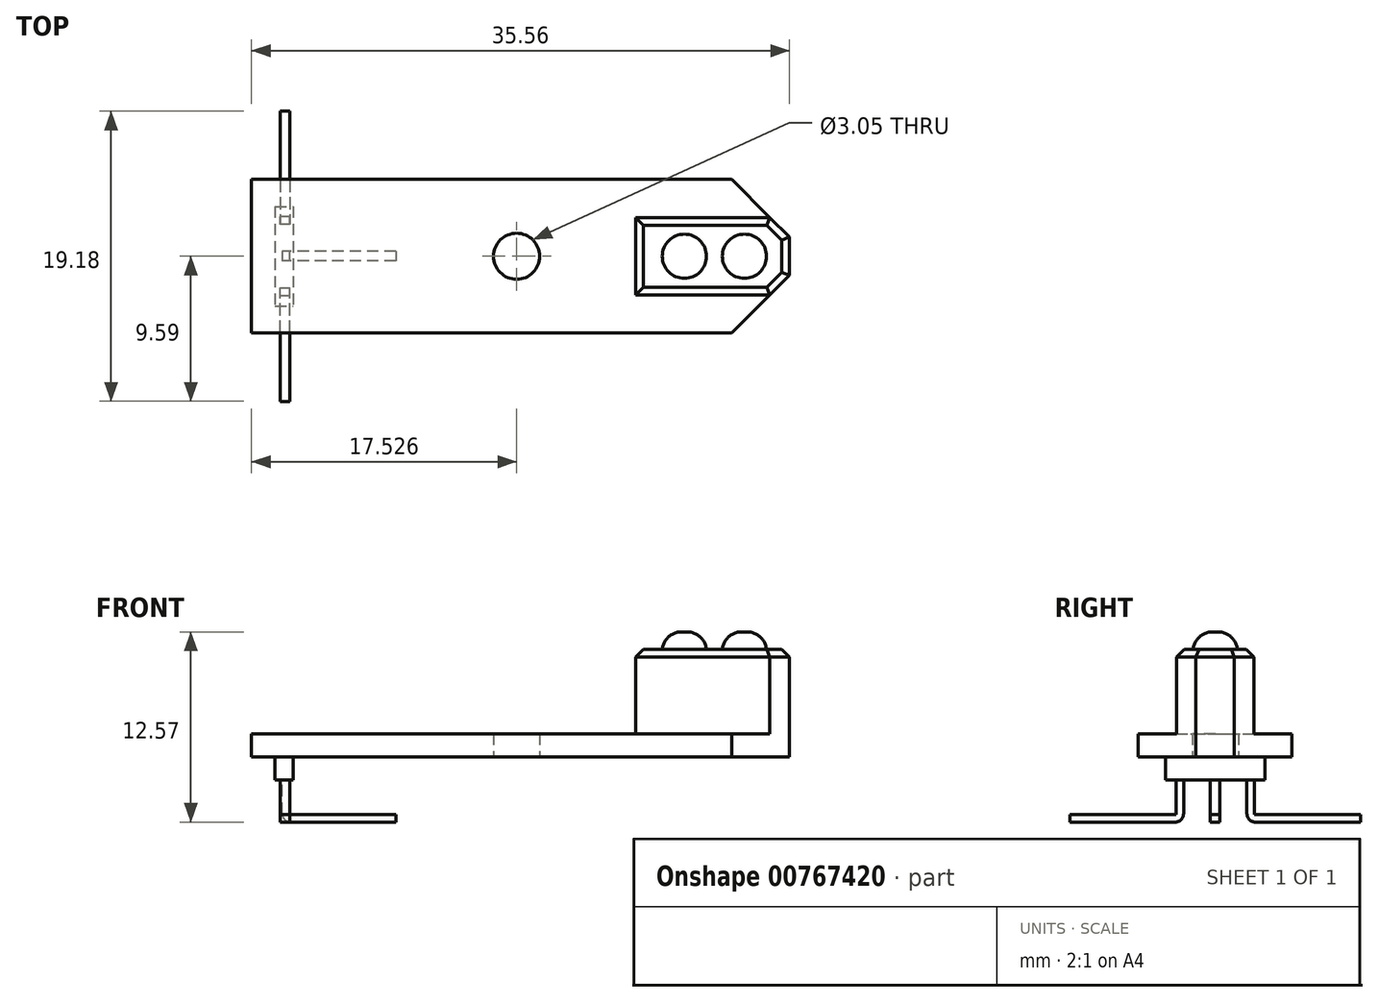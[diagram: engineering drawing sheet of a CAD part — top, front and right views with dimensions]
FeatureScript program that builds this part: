
annotation { "Feature Type Name" : "Feature", "Feature Type Description" : "" }
export const myFeature = defineFeature(function(context is Context, id is Id, definition is map)
    precondition{}
    {
        {
            var Q0;
            Q0=qCreatedBy(makeId("Top.planeOp"),FACE);
            var sketch = newSketch(context, id + "F0", { "sketchPlane" : qUnion([Q0])});
            skLineSegment(sketch, "E0.bottom", {"start": v(13.97, -5.08) * mm, "end": v(-17.78, -5.08) * mm});
            skLineSegment(sketch, "E0.top", {"start": v(13.97, 5.08) * mm, "end": v(-17.78, 5.08) * mm});
            skLineSegment(sketch, "E0.left", {"start": v(17.78, -1.27) * mm, "end": v(17.78, 1.27) * mm});
            skLineSegment(sketch, "E0.right", {"start": v(-17.78, -5.08) * mm, "end": v(-17.78, 5.08) * mm});
            skPoint(sketch, "E0.middle", {"position": v(0, 0) * mm});
            skLineSegment(sketch, "E1", {"start": v(13.97, 5.08) * mm, "end": v(17.78, 1.27) * mm});
            skLineSegment(sketch, "E2", {"start": v(0, 0) * mm, "end": v(10.97, 0) * mm, "construction": true});
            skLineSegment(sketch, "E3.MirrorCS", {"start": v(13.97, -5.08) * mm, "end": v(17.78, -1.27) * mm});
            skPoint(sketch, "E4.orphan", {"position": v(17.78, 5.08) * mm});
            skPoint(sketch, "E5.orphan", {"position": v(17.78, -5.08) * mm});
            skLineSegment(sketch, "E6.bottom", {"start": v(7.62, -2.57) * mm, "end": v(17.78, -2.57) * mm});
            skLineSegment(sketch, "E6.top", {"start": v(7.62, 2.57) * mm, "end": v(17.78, 2.57) * mm});
            skLineSegment(sketch, "E6.left", {"start": v(7.62, -2.57) * mm, "end": v(7.62, 2.57) * mm});
            skLineSegment(sketch, "E6.right", {"start": v(17.78, -2.57) * mm, "end": v(17.78, 2.57) * mm});
            skPoint(sketch, "E6.middle", {"position": v(12.7, 0) * mm});
            skPoint(sketch, "E6.middle.positionSnap0", {"position": v(5.48, 0) * mm});
            skPoint(sketch, "E6.centerSnap0", {"position": v(5.48, 0) * mm});
            skSolve(sketch);
        }
        {
            var Q0;
            {var subQ4=sQuery(id+"F0.wireOp",EDGE,"E0.bottom");Q0=makeQuery(id+"F0.imprint","IMPRINT",FACE,{"disambiguationData":[TD([[makeQuery(id+"F0.imprint","IMPRINT",EDGE,{"derivedFrom":subQ4}),-1.0]])]});}
            var Q1;
            {var subQ0=sQuery(id+"F0.wireOp",EDGE,"E6.left");Q1=makeQuery(id+"F0.imprint","IMPRINT",FACE,{"disambiguationData":[TD([[makeQuery(id+"F0.imprint","IMPRINT",EDGE,{"derivedFrom":subQ0}),-1.0]])]});}
            extrude(context, id + "F1", {"entities" : qUnion([Q0, Q1]), "oppositeDirection" : true, "depth" : 1.52 * mm});
        }
        {
            var Q0;
            {var subQ4=sQuery(id+"F0.wireOp",EDGE,"E0.bottom");Q0=makeQuery(id+"F0.imprint","IMPRINT",FACE,{"disambiguationData":[TD([[makeQuery(id+"F0.imprint","IMPRINT",EDGE,{"derivedFrom":subQ4}),-1.0]])]});}
            var sketch = newSketch(context, id + "F2", { "sketchPlane" : qUnion([Q0])});
            skLineSegment(sketch, "E7.0", {"start": v(17.78, -1.27) * mm, "end": v(17.78, 1.27) * mm});
            skLineSegment(sketch, "E8.0", {"start": v(7.62, 2.57) * mm, "end": v(16.48, 2.57) * mm});
            skLineSegment(sketch, "E9.0", {"start": v(7.62, -2.57) * mm, "end": v(16.48, -2.57) * mm});
            skLineSegment(sketch, "E10.0", {"start": v(7.62, -2.57) * mm, "end": v(7.62, 2.57) * mm});
            skLineSegment(sketch, "E11.0", {"start": v(16.48, -2.57) * mm, "end": v(17.78, -1.27) * mm});
            skLineSegment(sketch, "E12.0", {"start": v(16.48, 2.57) * mm, "end": v(17.78, 1.27) * mm});
            skPoint(sketch, "E13.orphan", {"position": v(13.97, 5.08) * mm});
            skPoint(sketch, "E14.orphan", {"position": v(17.78, 2.57) * mm});
            skPoint(sketch, "E15.orphan", {"position": v(17.78, -2.57) * mm});
            skPoint(sketch, "E16.orphan", {"position": v(13.97, -5.08) * mm});
            skSolve(sketch);
        }
        {
            var Q0;
            Q0=makeQuery(id+"F2.imprint","IMPRINT",FACE,{"disambiguationData":[TD([[makeQuery(id+"F2.imprint","IMPRINT",EDGE,{"derivedFrom":sQuery(id+"F2.wireOp",EDGE,"E7.0")}),1.0]])]});
            extrude(context, id + "F3", {"entities" : qUnion([Q0]), "operationType" : NewBodyOperationType.ADD, "depth" : 5.6 * mm});
        }
        {
            var Q0;
            Q0=makeQuery(id+"F3.opExtrude","CAP_FACE",FACE,{"disambiguationData":[OSD([sQuery(id+"F2.wireOp",EDGE,"E7.0"),sQuery(id+"F2.wireOp",EDGE,"E8.0"),sQuery(id+"F2.wireOp",EDGE,"E9.0"),sQuery(id+"F2.wireOp",EDGE,"E10.0"),sQuery(id+"F2.wireOp",EDGE,"E11.0"),sQuery(id+"F2.wireOp",EDGE,"E12.0")])],"isStart":false});
            var sketch = newSketch(context, id + "F4", { "sketchPlane" : qUnion([Q0])});
            skCircle(sketch, "E17", {"center": v(14.8, 0) * mm, "radius": 1.46 * mm});
            skCircle(sketch, "E18", {"center": v(10.83, 0) * mm, "radius": 1.46 * mm});
            skPoint(sketch, "E18.centerSnap0", {"position": v(7.62, 0) * mm});
            skSolve(sketch);
        }
        {
            var Q0;
            Q0=makeQuery(id+"F4.imprint","IMPRINT",FACE,{"disambiguationData":[TD([[makeQuery(id+"F4.imprint","IMPRINT",EDGE,{"derivedFrom":sQuery(id+"F4.wireOp",EDGE,"E18")}),1.0]])]});
            var Q1;
            Q1=makeQuery(id+"F4.imprint","IMPRINT",FACE,{"disambiguationData":[TD([[makeQuery(id+"F4.imprint","IMPRINT",EDGE,{"derivedFrom":sQuery(id+"F4.wireOp",EDGE,"E17")}),1.0]])]});
            extrude(context, id + "F5", {"entities" : qUnion([Q0, Q1]), "operationType" : NewBodyOperationType.ADD, "depth" : 1.14 * mm});
        }
        {
            var Q0;
            Q0=makeQuery(id+"F5.opExtrude","CAP_EDGE",EDGE,{"disambiguationData":[OSD([sQuery(id+"F4.wireOp",EDGE,"E18")])],"isStart":false});
            var Q1;
            Q1=makeQuery(id+"F5.opExtrude","CAP_EDGE",EDGE,{"disambiguationData":[OSD([sQuery(id+"F4.wireOp",EDGE,"E17")])],"isStart":false});
            fillet(context, id + "F6", {"entities" : qUnion([Q0, Q1]), "radius" : 1.27 * mm, "tangentPropagation" : true, "allowEdgeOverflow" : false});
        }
        {
            var Q0;
            Q0=makeQuery(id+"F3.opExtrude","CAP_EDGE",EDGE,{"disambiguationData":[OSD([sQuery(id+"F2.wireOp",EDGE,"E9.0")])],"isStart":false});
            var Q1;
            Q1=makeQuery(id+"F3.opExtrude","CAP_EDGE",EDGE,{"disambiguationData":[OSD([sQuery(id+"F2.wireOp",EDGE,"E8.0")])],"isStart":false});
            var Q2;
            Q2=makeQuery(id+"F3.opExtrude","CAP_EDGE",EDGE,{"disambiguationData":[OSD([sQuery(id+"F2.wireOp",EDGE,"E10.0")])],"isStart":false});
            var Q3;
            Q3=makeQuery(id+"F3.opExtrude","CAP_EDGE",EDGE,{"disambiguationData":[OSD([sQuery(id+"F2.wireOp",EDGE,"E7.0")])],"isStart":false});
            var Q4;
            Q4=makeQuery(id+"F3.opExtrude","CAP_EDGE",EDGE,{"disambiguationData":[OSD([sQuery(id+"F2.wireOp",EDGE,"E11.0")])],"isStart":false});
            var Q5;
            Q5=makeQuery(id+"F3.opExtrude","CAP_EDGE",EDGE,{"disambiguationData":[OSD([sQuery(id+"F2.wireOp",EDGE,"E12.0")])],"isStart":false});
            chamfer(context, id + "F7", {"entities" : qUnion([Q0, Q1, Q2, Q3, Q4, Q5]), "width" : 0.5 * mm, "tangentPropagation" : true});
        }
        {
            var Q0;
            Q0=qCreatedBy(makeId("Front.planeOp"),FACE);
            var sketch = newSketch(context, id + "F8", { "sketchPlane" : qUnion([Q0])});
            skLineSegment(sketch, "E19", {"start": v(-22.86, -5.84) * mm, "end": v(-15.92, -5.84) * mm});
            skLineSegment(sketch, "E20", {"start": v(-15.36, -5.29) * mm, "end": v(-15.36, -1.17) * mm});
            skPoint(sketch, "E21.visualSharp", {"position": v(-15.36, -5.84) * mm});
            skArc(sketch, "E21.filletArc", {"start": v(-15.92, -5.84) * mm, "mid": v(-15.52, -5.68) * mm, "end": v(-15.36, -5.29) * mm});
            skLineSegment(sketch, "E22.0", {"start": v(-22.86, -5.33) * mm, "end": v(-15.87, -5.33) * mm});
            skLineSegment(sketch, "E23.0", {"start": v(-15.87, -5.33) * mm, "end": v(-15.87, -1.17) * mm});
            skLineSegment(sketch, "E24", {"start": v(-15.87, -1.17) * mm, "end": v(-15.36, -1.17) * mm});
            skLineSegment(sketch, "E25", {"start": v(-22.86, -5.84) * mm, "end": v(-22.86, -5.33) * mm});
            skSolve(sketch);
        }
        {
            var Q0;
            Q0=makeQuery(id+"F8.imprint","IMPRINT",FACE,{"disambiguationData":[TD([[makeQuery(id+"F8.imprint","IMPRINT",EDGE,{"derivedFrom":sQuery(id+"F8.wireOp",EDGE,"E19")}),1.0]])]});
            extrude(context, id + "F9", {"entities" : qUnion([Q0]), "depth" : 0.64 * mm, "symmetric" : true});
        }
        {
            var Q0;
            Q0=makeQuery(id+"F9.opExtrude","SWEPT_BODY",BODY,{"disambiguationData":[OSD([sQuery(id+"F8.wireOp",EDGE,"E19"),sQuery(id+"F8.wireOp",EDGE,"E20"),sQuery(id+"F8.wireOp",EDGE,"E21.filletArc"),sQuery(id+"F8.wireOp",EDGE,"E22.0"),sQuery(id+"F8.wireOp",EDGE,"E23.0"),sQuery(id+"F8.wireOp",EDGE,"E24"),sQuery(id+"F8.wireOp",EDGE,"E25")])]});
            transform(context, id + "F10", {"entities" : qUnion([Q0]), "transformType" : TransformType.TRANSLATION_3D, "dx" : 0 * mm, "dy" : -2.92 * mm, "dz" : 0 * mm, "makeCopy" : true});
        }
        {
            var Q0;
            Q0=makeQuery(id+"F10.opPattern","COPY",BODY,{"derivedFrom":makeQuery(id+"F9.opExtrude","SWEPT_BODY",BODY,{"disambiguationData":[OSD([sQuery(id+"F8.wireOp",EDGE,"E19"),sQuery(id+"F8.wireOp",EDGE,"E20"),sQuery(id+"F8.wireOp",EDGE,"E21.filletArc"),sQuery(id+"F8.wireOp",EDGE,"E22.0"),sQuery(id+"F8.wireOp",EDGE,"E23.0"),sQuery(id+"F8.wireOp",EDGE,"E24"),sQuery(id+"F8.wireOp",EDGE,"E25")])]}),"instanceName":"1"});
            var Q1;
            Q1=makeQuery(id+"F10.opPattern","COPY",EDGE,{"derivedFrom":makeQuery(id+"F9.opExtrude","CAP_EDGE",EDGE,{"disambiguationData":[OSD([sQuery(id+"F8.wireOp",EDGE,"E23.0")])],"isStart":true}),"instanceName":"1"});
            transform(context, id + "F11", {"entities" : qUnion([Q0]), "transformType" : TransformType.ROTATION, "transformAxis" : qUnion([Q1]), "angle" : 90 * degree, "makeCopy" : false});
        }
        {
            var Q0;
            Q0=makeQuery(id+"F10.opPattern","COPY",BODY,{"derivedFrom":makeQuery(id+"F9.opExtrude","SWEPT_BODY",BODY,{"disambiguationData":[OSD([sQuery(id+"F8.wireOp",EDGE,"E19"),sQuery(id+"F8.wireOp",EDGE,"E20"),sQuery(id+"F8.wireOp",EDGE,"E21.filletArc"),sQuery(id+"F8.wireOp",EDGE,"E22.0"),sQuery(id+"F8.wireOp",EDGE,"E23.0"),sQuery(id+"F8.wireOp",EDGE,"E24"),sQuery(id+"F8.wireOp",EDGE,"E25")])]}),"instanceName":"1"});
            var Q1;
            Q1=qCreatedBy(makeId("Front.planeOp"),FACE);
            mirror(context, id + "F12", {"operationType" : NewBodyOperationType.ADD, "entities" : qUnion([Q0]), "mirrorPlane" : qUnion([Q1])});
        }
        {
            var Q0;
            Q0=makeQuery(id+"F9.opExtrude","SWEPT_BODY",BODY,{"disambiguationData":[OSD([sQuery(id+"F8.wireOp",EDGE,"E19"),sQuery(id+"F8.wireOp",EDGE,"E20"),sQuery(id+"F8.wireOp",EDGE,"E21.filletArc"),sQuery(id+"F8.wireOp",EDGE,"E22.0"),sQuery(id+"F8.wireOp",EDGE,"E23.0"),sQuery(id+"F8.wireOp",EDGE,"E24"),sQuery(id+"F8.wireOp",EDGE,"E25")])]});
            var Q1;
            Q1=makeQuery(id+"F9.opExtrude","CAP_EDGE",EDGE,{"disambiguationData":[OSD([sQuery(id+"F8.wireOp",EDGE,"E23.0")])],"isStart":true});
            transform(context, id + "F13", {"entities" : qUnion([Q0]), "transformType" : TransformType.ROTATION, "transformAxis" : qUnion([Q1]), "angle" : 180 * degree, "makeCopy" : false});
        }
        {
            var Q0;
            Q0=makeQuery(id+"F9.opExtrude","SWEPT_BODY",BODY,{"disambiguationData":[OSD([sQuery(id+"F8.wireOp",EDGE,"E19"),sQuery(id+"F8.wireOp",EDGE,"E20"),sQuery(id+"F8.wireOp",EDGE,"E21.filletArc"),sQuery(id+"F8.wireOp",EDGE,"E22.0"),sQuery(id+"F8.wireOp",EDGE,"E23.0"),sQuery(id+"F8.wireOp",EDGE,"E24"),sQuery(id+"F8.wireOp",EDGE,"E25")])]});
            transform(context, id + "F14", {"entities" : qUnion([Q0]), "transformType" : TransformType.TRANSLATION_3D, "dx" : .635 * mm, "dy" : -.635 * mm, "dz" : 0 * mm, "makeCopy" : false});
        }
        {
            var Q0;
            Q0=makeQuery(id+"F1.opExtrude","CAP_FACE",FACE,{"disambiguationData":[OSD([sQuery(id+"F0.wireOp",EDGE,"E0.bottom"),sQuery(id+"F0.wireOp",EDGE,"E0.top"),sQuery(id+"F0.wireOp",EDGE,"E0.right"),sQuery(id+"F0.wireOp",EDGE,"E1"),sQuery(id+"F0.wireOp",EDGE,"E3.MirrorCS"),sQuery(id+"F0.wireOp",EDGE,"E6.right")])],"isStart":false});
            var sketch = newSketch(context, id + "F15", { "sketchPlane" : qUnion([Q0])});
            skLineSegment(sketch, "E26.bottom", {"start": v(-16.22, -3.3) * mm, "end": v(-15.02, -3.3) * mm});
            skLineSegment(sketch, "E26.top", {"start": v(-16.22, 3.3) * mm, "end": v(-15.02, 3.3) * mm});
            skLineSegment(sketch, "E26.left", {"start": v(-16.22, -3.3) * mm, "end": v(-16.22, 3.3) * mm});
            skLineSegment(sketch, "E26.right", {"start": v(-15.02, -3.3) * mm, "end": v(-15.02, 3.3) * mm});
            skPoint(sketch, "E26.middle", {"position": v(-15.62, 0) * mm});
            skSolve(sketch);
        }
        {
            var Q0;
            Q0=makeQuery(id+"F15.imprint","IMPRINT",FACE,{"disambiguationData":[TD([[makeQuery(id+"F15.imprint","IMPRINT",EDGE,{"derivedFrom":sQuery(id+"F15.wireOp",EDGE,"E26.bottom")}),1.0]])]});
            extrude(context, id + "F16", {"entities" : qUnion([Q0]), "operationType" : NewBodyOperationType.ADD, "depth" : 1.52 * mm});
        }
        {
            var Q0;
            Q0=makeQuery(id+"F1.opExtrude","CAP_FACE",FACE,{"disambiguationData":[OSD([sQuery(id+"F0.wireOp",EDGE,"E0.bottom"),sQuery(id+"F0.wireOp",EDGE,"E0.top"),sQuery(id+"F0.wireOp",EDGE,"E0.right"),sQuery(id+"F0.wireOp",EDGE,"E1"),sQuery(id+"F0.wireOp",EDGE,"E3.MirrorCS"),sQuery(id+"F0.wireOp",EDGE,"E6.right")])],"isStart":false});
            var sketch = newSketch(context, id + "F17", { "sketchPlane" : qUnion([Q0])});
            skCircle(sketch, "E27", {"center": v(-0.25, 0) * mm, "radius": 1.52 * mm});
            skSolve(sketch);
        }
        {
            var Q0;
            Q0=makeQuery(id+"F17.imprint","IMPRINT",FACE,{"disambiguationData":[TD([[makeQuery(id+"F17.imprint","IMPRINT",EDGE,{"derivedFrom":sQuery(id+"F17.wireOp",EDGE,"E27")}),1.0]])]});
            extrude(context, id + "F18", {"entities" : qUnion([Q0]), "operationType" : NewBodyOperationType.REMOVE, "oppositeDirection" : true, "depth" : 25.4 * mm});
        }
    });
